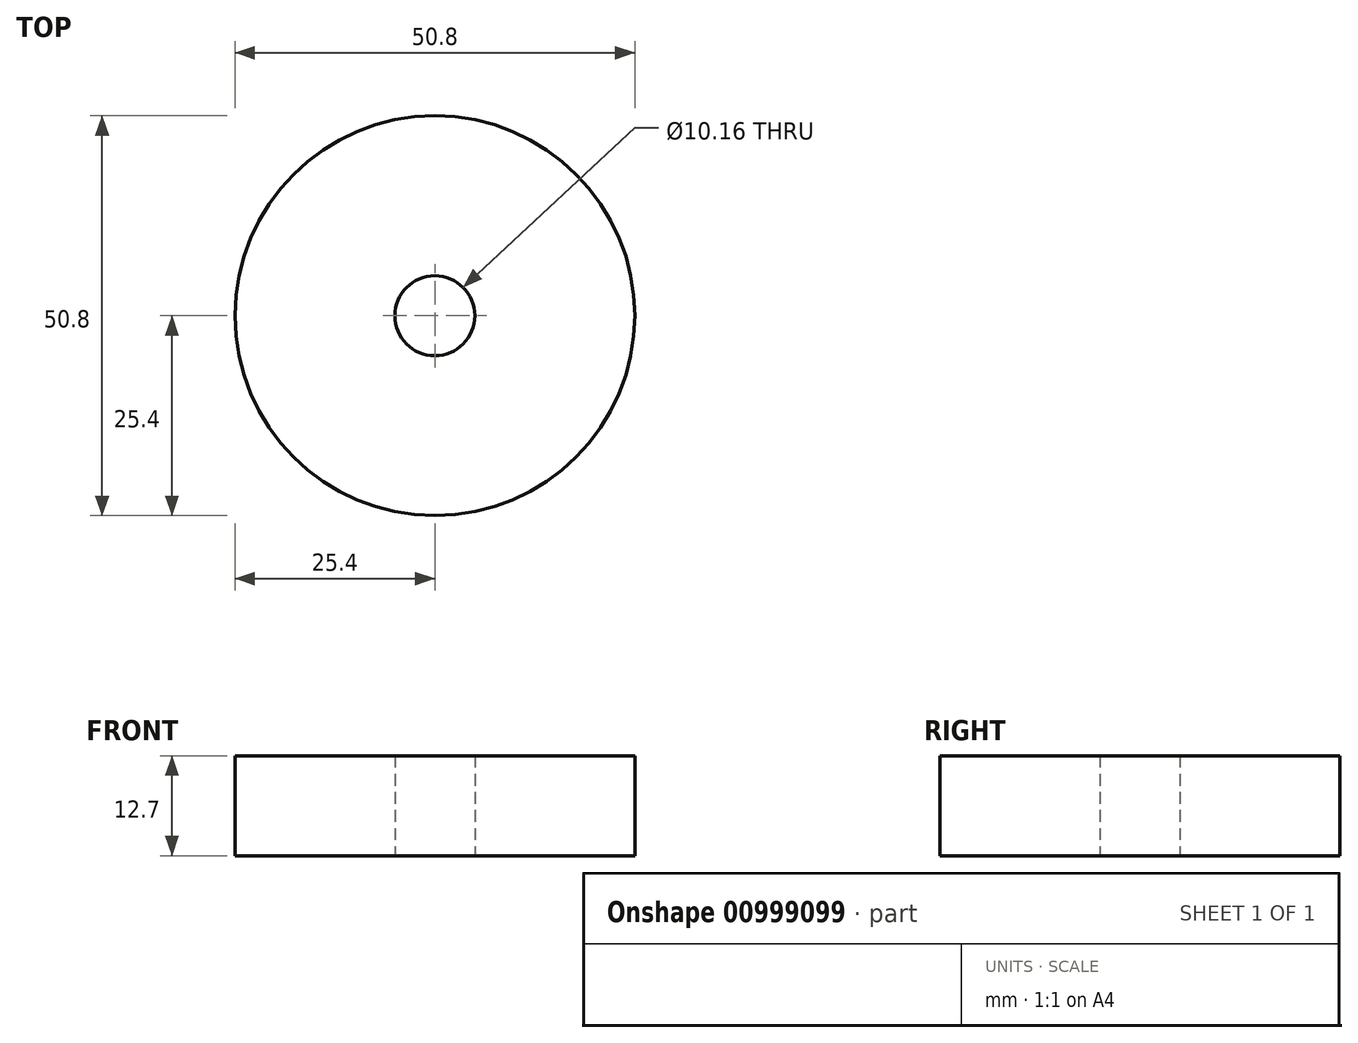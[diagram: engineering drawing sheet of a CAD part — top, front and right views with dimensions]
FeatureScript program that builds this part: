
annotation { "Feature Type Name" : "Feature", "Feature Type Description" : "" }
export const myFeature = defineFeature(function(context is Context, id is Id, definition is map)
    precondition{}
    {
        {
            var Q0;
            Q0=qCreatedBy(makeId("Top.planeOp"),FACE);
            var sketch = newSketch(context, id + "F0", { "sketchPlane" : qUnion([Q0])});
            skCircle(sketch, "E0", {"center": v(0, 0) * mm, "radius": 25.4 * mm});
            skCircle(sketch, "E1", {"center": v(0, 0) * mm, "radius": 5.08 * mm});
            skSolve(sketch);
        }
        {
            var Q0;
            Q0 = qSketchRegion(id + "F0", true);
            extrude(context, id + "F1", {"entities" : qUnion([Q0]), "depth" : 12.7 * mm, "offsetDistance" : 25.4 * mm});
        }
    });
